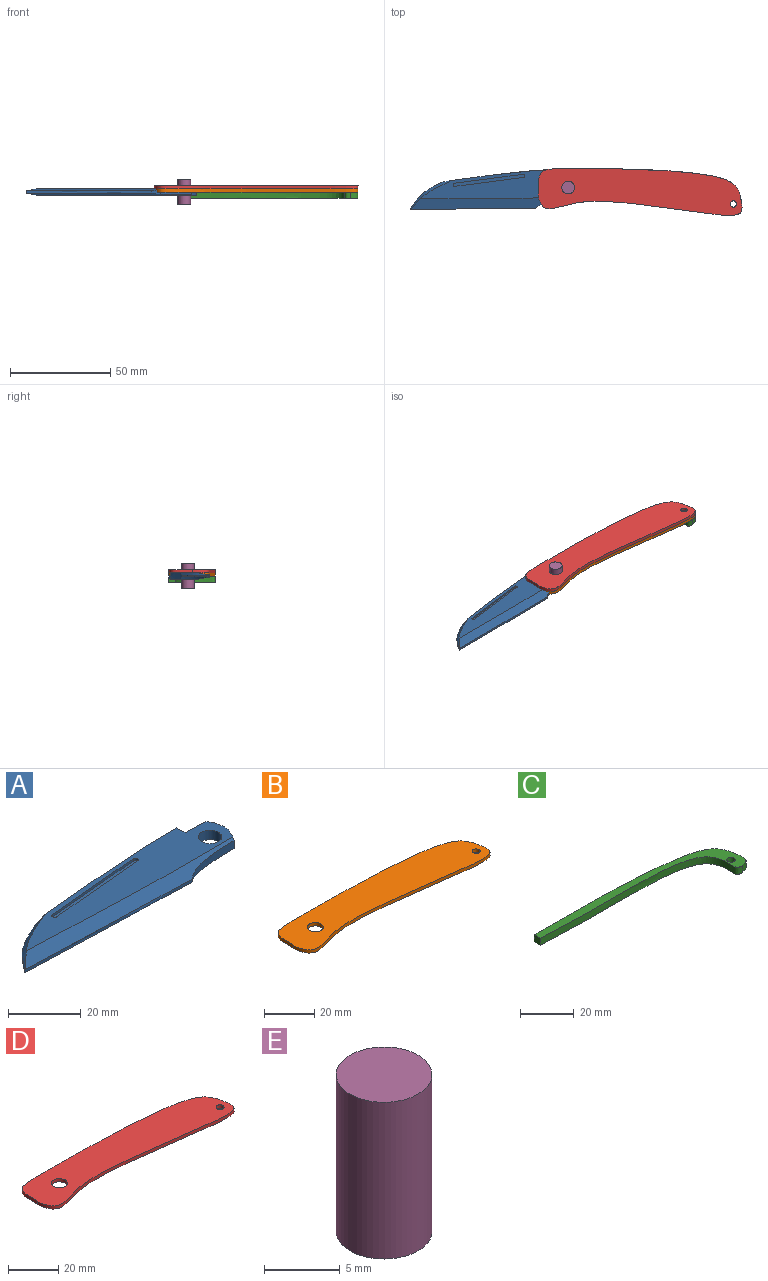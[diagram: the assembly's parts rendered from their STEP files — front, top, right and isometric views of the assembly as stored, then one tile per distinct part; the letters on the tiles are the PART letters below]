
ASSEMBLY  parts=5 mates=4
PART A: 25 faces, bbox 92.1x19.1x3.2 mm
  f0: extruded ~62.88x1.9mm, area 63.8mm2, adj f1,f7,f11,f12,f13,f14
  f1: extruded ~20.15x3.92mm, area 47.6mm2, adj f0,f2,f11,f12
  f2: extruded ~11.58x3.18mm, area 39.4mm2, adj f1,f3,f9,f10,f11,f12
  f3: extruded ~7.76x3.18mm, area 24.7mm2, adj f2,f4,f9,f10
  f4: plane 3.19x3.18mm, normal (1,0,0), area 10.1mm2, adj f3,f5,f9,f10
  f5: extruded ~13.11x3.18mm, area 41.6mm2, adj f4,f6,f9,f10
  f6: extruded ~46.49x4.01mm, area 142.6mm2, adj f5,f7,f9,f10,f13,f14
  f7: extruded ~16.4x12.87mm, area 13.5mm2, adj f0,f6,f13,f14
  f8: cylinder r=3.17mm len=6.35mm, axis (0,0,-1), area 63.3mm2, adj f9,f10
  f9: plane 80.47x14.09mm, normal (0,0,1), area 757.1mm2, adj f2,f3,f4,f5,f6,f8,f12,f14
  f10: plane 80.47x14.09mm, normal (0,0,-1), area 757.1mm2, adj f2,f3,f4,f5,f6,f8,f11,f13
  f11: bspline ~92.14x7.07mm, area 354.2mm2, adj f0,f1,f2,f10,f13
  f12: bspline ~92.14x7.07mm, area 354.2mm2, adj f0,f1,f2,f9,f14
  f13: bspline ~23.12x17mm, area 36.3mm2, adj f0,f6,f7,f10,f11
  f14: bspline ~23.12x17mm, area 36.3mm2, adj f0,f6,f7,f9,f12
  f15: plane 34.42x3.12mm, normal (0.09,-1,0), area 27.4mm2, adj f9,f16,f18,f19
  f16: cylinder r=0.79mm len=1.58mm, axis (0,0,1), area 2mm2, adj f9,f15,f17,f19
  f17: plane 34.42x3.12mm, normal (-0.09,1,0), area 27.4mm2, adj f9,f16,f18,f19
  f18: cylinder r=0.79mm len=1.58mm, axis (0,0,1), area 2mm2, adj f9,f15,f17,f19
  f19: plane 36x4.7mm, normal (0,0,1), area 56.8mm2, adj f15,f16,f17,f18
  f20: plane 34.42x3.12mm, normal (0.09,-1,0), area 27.4mm2, adj f10,f21,f23,f24
  f21: cylinder r=0.79mm len=1.58mm, axis (0,0,-1), area 2mm2, adj f10,f20,f22,f24
  f22: plane 34.42x3.12mm, normal (-0.09,1,0), area 27.4mm2, adj f10,f21,f23,f24
  f23: cylinder r=0.79mm len=1.58mm, axis (0,0,-1), area 2mm2, adj f10,f20,f22,f24
  f24: plane 36x4.7mm, normal (0,0,-1), area 56.8mm2, adj f20,f21,f22,f23
PART B: 6 faces, bbox 102.2x26.3x1.6 mm
  f0: extruded ~101.6x17.65mm, area 189mm2, adj f1,f2,f3
  f1: extruded ~101.7x11.18mm, area 177.8mm2, adj f0,f2,f3
  f2: plane 102.2x26.33mm, normal (0,0,-1), area 1751.5mm2, adj f0,f1,f4,f5
  f3: plane 102.2x26.33mm, normal (0,0,1), area 1751.5mm2, adj f0,f1,f4,f5
  f4: cylinder r=3.17mm len=6.35mm, axis (0,0,1), area 31.7mm2, adj f2,f3
  f5: cylinder r=1.59mm len=3.18mm, axis (0,0,1), area 15.8mm2, adj f2,f3
PART C: 7 faces, bbox 90.5x23.6x3.2 mm
  f0: extruded ~86.24x20.03mm, area 310.8mm2, adj f1,f3,f4,f5
  f1: extruded ~5.59x3.99mm, area 25.5mm2, adj f0,f2,f4,f5
  f2: extruded ~90.12x17.65mm, area 311.1mm2, adj f1,f3,f4,f5
  f3: plane 3.19x3.18mm, normal (-1,0,0), area 10.1mm2, adj f0,f2,f4,f5
  f4: plane 90.54x23.6mm, normal (0,0,1), area 375.9mm2, adj f0,f1,f2,f3,f6
  f5: plane 90.54x23.6mm, normal (0,0,-1), area 375.9mm2, adj f0,f1,f2,f3,f6
  f6: cylinder r=1.59mm len=3.18mm, axis (0,0,1), area 31.7mm2, adj f4,f5
PART D: 6 faces, bbox 102.2x26.3x1.6 mm
  f0: extruded ~101.6x17.65mm, area 189mm2, adj f1,f2,f3
  f1: extruded ~101.7x11.18mm, area 177.8mm2, adj f0,f2,f3
  f2: plane 102.2x26.33mm, normal (0,0,1), area 1751.5mm2, adj f0,f1,f4,f5
  f3: plane 102.2x26.33mm, normal (0,0,-1), area 1751.5mm2, adj f0,f1,f4,f5
  f4: cylinder r=3.17mm len=6.35mm, axis (0,0,1), area 31.7mm2, adj f2,f3
  f5: cylinder r=1.59mm len=3.18mm, axis (0,0,1), area 15.8mm2, adj f2,f3
PART E: 3 faces, bbox 6.4x6.4x12.7 mm
  f0: cylinder r=3.17mm len=12.7mm, axis (0,0,-1), area 253.4mm2, adj f1,f2
  f1: plane 6.35x6.35mm, normal (0,0,1), area 31.7mm2, adj f0
  f2: plane 6.35x6.35mm, normal (0,0,-1), area 31.7mm2, adj f0
PLACE A rot(axis=(0,0,1),2.3deg) t=(75.76,-24.09,-8.06)mm
PLACE B rot(axis=(0.41,0.03,-0.91),0deg) t=(75.68,-25.52,-4.89)mm
PLACE C rot(axis=(0.41,0.03,-0.91),0deg) t=(75.68,-25.52,-9.65)mm
PLACE D rot(axis=(0.41,0.03,-0.91),0deg) t=(75.68,-25.52,-8.06)mm
PLACE E rot(axis=(-0.71,0.71,0),180deg) t=(42.41,-58.79,-8.06)mm
MATE fastened B.f5 <-> C.f6  axis (0,0,-1) through (122.26,-31.04,-8.06)mm
MATE fastened E.f0 <-> D.f4  axis (0,0,1) through (39.76,-22.87,-1.71)mm
MATE revolute A.f8 <-> E.f0  axis (0,0,-1) through (39.76,-22.87,-8.06)mm
MATE fastened D.f5 <-> B.f5  axis (0,0,-1) through (122.26,-31.04,-6.47)mm
